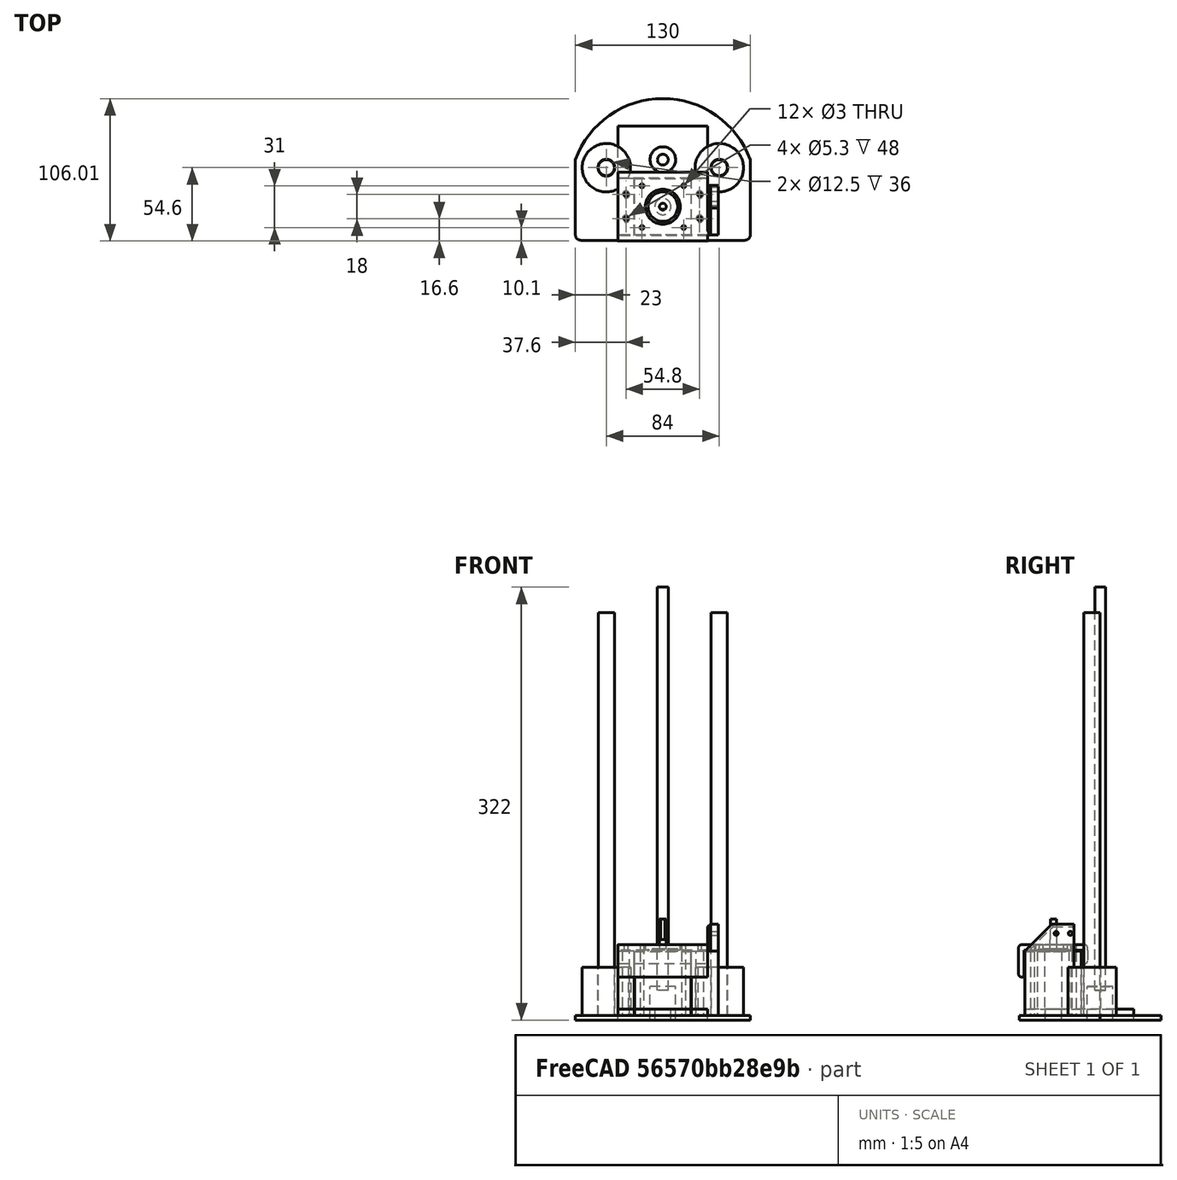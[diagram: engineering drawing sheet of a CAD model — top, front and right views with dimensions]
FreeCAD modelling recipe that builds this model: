
FCSTD DOCUMENT  (FreeCAD 0.18R16110 (Git))
Label: jSCARA-V2
License: All rights reserved
LicenseURL: http://en.wikipedia.org/wiki/All_rights_reserved
objects: PartDesign::Pad×12, Sketcher::SketchObject×7, Part::Cylinder×4, PartDesign::Fillet×3, PartDesign::Body×3, App::Part×3, PartDesign::Mirrored×2, Part::FeaturePython×2, PartDesign::Chamfer×2, Mesh::Feature×1, PartDesign::Pocket×1
note: 49 computed .brp shape members not serialized (recipe doc carries the construction recipe); baked Part::Feature solids carry a one-line shape summary decoded from their .brp

FEATURE [Sketcher::SketchObject] Sketch
  MapMode = 5
  Support = -> [XY_Plane]
  sketch-geometry (4):
    g0: LineSegment StartX=-65 StartY=-3e-15 StartZ=0 EndX=-65 EndY=-60 EndZ=0
    g1: LineSegment StartX=-65 StartY=-60 StartZ=0 EndX=65 EndY=-60 EndZ=0
    g2: LineSegment StartX=65 StartY=-60 StartZ=0 EndX=65 EndY=0 EndZ=0
    g3: ArcOfCircle CenterX=-9e-15 CenterY=-23.8163 CenterZ=0 NormalX=0 NormalY=0 NormalZ=1 AngleXU=0 Radius=69.2258 StartAngle=0.351214 EndAngle=2.79038
  constraints (11):
    c: Coincident(g0,g1)
    c: Coincident(g1,g2)
    c: Vertical(g2)
    c: Vertical(g0)
    c: Symmetric(g1,g0,g-2)
    c: DistanceX(g1,g1) = 130
    c: Coincident(g3,g2)
    c: Coincident(g3,g0)
    c: Equal(g0,g2)
    c: DistanceY(g2,g2) = 60
    c: PointOnObject(g2,g-1)
FEATURE [PartDesign::Pad] Pad  label="Base"
  Length = 3.4
  Length2 = 100
  Profile = -> Sketch
  Type = 0
FEATURE [Part::Cylinder] Cylinder  label="R Rail"
  Angle = 360
  AttacherType = Attacher::AttachEngine3D
  Height = 300
  Placement = pos=(42,-6,3) rot=(0,0,1;0rad)
  Radius = 6
FEATURE [Sketcher::SketchObject] Sketch001
  MapMode = 5
  Placement = pos=(0,0,3.4) rot=(0,0,1;0rad)
  Support = -> [Pad]
  sketch-geometry (2):
    g0: Circle CenterX=42 CenterY=-6 CenterZ=0 NormalX=0 NormalY=0 NormalZ=1 AngleXU=0 Radius=6.25
    g1: Circle CenterX=42 CenterY=-6 CenterZ=0 NormalX=0 NormalY=0 NormalZ=1 AngleXU=0 Radius=18
  constraints (5):
    c: Radius(g0) = 6.25
    c: Coincident(g1,g0)
    c: Radius(g1) = 18
    c: DistanceY(g0,g-1) = 6
    c: DistanceX(g-1,g0) = 42
FEATURE [PartDesign::Fillet] Fillet
  Base = -> Pad [Edge5,Edge2]
  BaseFeature = -> Pad
  Radius = 4
FEATURE [PartDesign::Pad] Pad001  label="Rod Holder R"
  BaseFeature = -> Fillet
  Length = 36
  Length2 = 100
  Profile = -> Sketch001
  Type = 0
FEATURE [PartDesign::Mirrored] Mirrored  label="Rod Holder L"
  BaseFeature = -> Pad001
  MirrorPlane = -> YZ_Plane
  Originals = -> [Pad001]
FEATURE [Part::FeaturePython] b_NEMASteppper__42x48__001_  label="NEMASteppper (42x48)_001"  # a2plus imported part (geometry in sourceFile) (typed FeaturePython)
  Placement = pos=(0,-35,3) rot=(0,0,1;0rad)
  a2p_Version = V0.1
  fixedPosition = true
  sourceFile = .\NEMASteppper (42x48).FCStd
  subassemblyImport = false
  timeLastImport = 1.55797e+09
  updateColors = true
FEATURE [Part::Cylinder] Cylinder001  label="L Rail"
  Angle = 360
  AttacherType = Attacher::AttachEngine3D
  Height = 300
  Placement = pos=(-42,-6,3) rot=(0,0,1;0rad)
  Radius = 6
FEATURE [Sketcher::SketchObject] Sketch002
  MapMode = 5
  Placement = pos=(0,0,3.4) rot=(0,0,1;0rad)
  Support = -> [Mirrored]
  sketch-geometry (7):
    g0: LineSegment StartX=-21.4 StartY=-56 StartZ=0 EndX=-21.4 EndY=-14 EndZ=0
    g1: LineSegment StartX=-21.4 StartY=-14 StartZ=0 EndX=-33.4 EndY=-14 EndZ=0
    g2: LineSegment StartX=-33.4 StartY=-14 StartZ=0 EndX=-33.4 EndY=-56 EndZ=0
    g3: LineSegment StartX=-33.4 StartY=-56 StartZ=0 EndX=-21.4 EndY=-56 EndZ=0
    g4: Circle CenterX=-27.4 CenterY=-26 CenterZ=0 NormalX=0 NormalY=0 NormalZ=1 AngleXU=0 Radius=2.65
    g5: Circle CenterX=-27.4 CenterY=-44 CenterZ=0 NormalX=0 NormalY=0 NormalZ=1 AngleXU=0 Radius=2.65
    g6: LineSegment [constr] StartX=-27.4 StartY=-14 StartZ=0 EndX=-27.4 EndY=-56 EndZ=0
  constraints (21):
    c: Vertical(g0)
    c: Coincident(g0,g1)
    c: Horizontal(g1)
    c: Coincident(g1,g2)
    c: Vertical(g2)
    c: Coincident(g2,g3)
    c: Coincident(g3,g0)
    c: Horizontal(g3)
    c: DistanceY(g0,g-1) = 14
    c: DistanceY(g0,g0) = 42
    c: DistanceX(g1,g1) = 12
    c: DistanceX(g0,g-1) = 21.4
    c: DistanceY(g4,g1) = 12
    c: Equal(g4,g5) = 3
    c: PointOnObject(g6,g1)
    c: Symmetric(g0,g2,g6)
    c: PointOnObject(g5,g6)
    c: PointOnObject(g4,g6)
    c: PointOnObject(g6,g3)
    c: DistanceY(g2,g5) = 12
    c: Diameter(g4) = 5.3
FEATURE [PartDesign::Pad] Pad002
  BaseFeature = -> Mirrored
  Length = 48
  Length2 = 100
  Profile = -> Sketch002
  Type = 0
FEATURE [PartDesign::Mirrored] Mirrored001
  BaseFeature = -> Pad002
  MirrorPlane = -> Sketch002 [V_Axis]
  Originals = -> [Pad002]
FEATURE [Sketcher::SketchObject] Sketch003
  MapMode = 5
  Support = -> [XY_Plane002]
  sketch-geometry (14):
    g0: Circle CenterX=-27.4 CenterY=-26 CenterZ=0 NormalX=0 NormalY=0 NormalZ=1 AngleXU=0 Radius=1.5
    g1: Circle CenterX=0 CenterY=-35 CenterZ=0 NormalX=0 NormalY=0 NormalZ=1 AngleXU=0 Radius=13
    g2: LineSegment StartX=-33.4 StartY=-14 StartZ=0 EndX=33.4 EndY=-14 EndZ=0
    g3: LineSegment StartX=33.4 StartY=-14 StartZ=0 EndX=33.4 EndY=-56 EndZ=0
    g4: LineSegment StartX=33.4 StartY=-56 StartZ=0 EndX=-33.4 EndY=-56 EndZ=0
    g5: LineSegment StartX=-33.4 StartY=-56 StartZ=0 EndX=-33.4 EndY=-14 EndZ=0
    g6: Circle CenterX=27.4 CenterY=-26 CenterZ=0 NormalX=0 NormalY=0 NormalZ=1 AngleXU=0 Radius=1.5
    g7: Circle CenterX=27.4 CenterY=-44 CenterZ=0 NormalX=0 NormalY=0 NormalZ=1 AngleXU=0 Radius=1.5
    g8: Circle CenterX=-27.4 CenterY=-44 CenterZ=0 NormalX=0 NormalY=0 NormalZ=1 AngleXU=0 Radius=1.5
    g9: LineSegment [constr] StartX=-27.4 StartY=-26 StartZ=0 EndX=-27.4 EndY=-44 EndZ=0
    g10: Circle CenterX=-15.5 CenterY=-50.5 CenterZ=0 NormalX=0 NormalY=0 NormalZ=1 AngleXU=0 Radius=1.5
    g11: Circle CenterX=15.5 CenterY=-50.5 CenterZ=0 NormalX=0 NormalY=0 NormalZ=1 AngleXU=0 Radius=1.5
    g12: Circle CenterX=-15.5 CenterY=-19.5 CenterZ=0 NormalX=0 NormalY=0 NormalZ=1 AngleXU=0 Radius=1.5
    g13: Circle CenterX=15.5 CenterY=-19.5 CenterZ=0 NormalX=0 NormalY=0 NormalZ=1 AngleXU=0 Radius=1.5
  constraints (36):
    c: PointOnObject(g1,g-2)
    c: Radius(g1) = 13
    c: DistanceY(g1,g-1) = 35
    c: Coincident(g2,g3)
    c: Coincident(g3,g4)
    c: Coincident(g4,g5)
    c: Coincident(g5,g2)
    c: Horizontal(g4)
    c: Vertical(g3)
    c: Vertical(g5)
    c: DistanceX(g2,g2) = 66.8
    c: Symmetric(g2,g2,g-2)
    c: DistanceY(g3,g3) = 42
    c: DistanceY(g2,g-1) = 14
    c: Equal(g0,g6) = 3
    c: Symmetric(g6,g0,g-2)
    c: Equal(g0,g8) = 3
    c: Equal(g8,g7) = 3
    c: DistanceY(g1,g6) = 9
    c: DistanceY(g8,g0) = 18
    c: Symmetric(g7,g8,g-2)
    c: Coincident(g9,g0)
    c: Coincident(g9,g8)
    c: Vertical(g9)
    c: Radius(g10) = 1.5
    c: Equal(g10,g11) = 3
    c: Symmetric(g10,g11,g-2)
    c: DistanceX(g10,g11) = 31
    c: DistanceY(g3,g11) = 5.5
    c: Equal(g10,g12) = 3
    c: Symmetric(g12,g13,g-2)
    c: DistanceX(g12,g13) = 31
    c: DistanceY(g10,g12) = 31
    c: Equal(g13,g12)
    c: DistanceX(g4,g8) = 6
    c: Radius(g0) = 1.5
FEATURE [PartDesign::Pad] Pad003
  Length = 4
  Length2 = 100
  Profile = -> Sketch003
  Type = 0
FEATURE [PartDesign::Fillet] Fillet002
  Base = -> Mirrored001 [Edge50,Edge37]
  BaseFeature = -> Mirrored001
  Radius = 2
FEATURE [PartDesign::Pad] Pad004
  BaseFeature = -> Pad003
  Length = 0.6
  Length2 = 100
  Profile = -> Pad003 [Face3]
  Type = 0
FEATURE [PartDesign::Pad] Pad005
  BaseFeature = -> Pad004
  Length = 4
  Length2 = 100
  Profile = -> Pad004 [Face19]
  Type = 0
FEATURE [PartDesign::Pad] Pad006
  BaseFeature = -> Pad005
  Length = 20
  Length2 = 100
  Profile = -> Pad005 [Face21]
  Type = 0
FEATURE [PartDesign::Pad] Pad007
  BaseFeature = -> Pad006
  Length = 0.6
  Length2 = 100
  Profile = -> Pad006 [Face1]
  Type = 0
FEATURE [PartDesign::Pad] Pad008
  BaseFeature = -> Pad007
  Length = 4
  Length2 = 100
  Profile = -> Pad007 [Face11]
  Type = 0
FEATURE [PartDesign::Pad] Pad009
  BaseFeature = -> Pad008
  Length = 10
  Length2 = 100
  Profile = -> Pad008 [Face28]
  Type = 0
FEATURE [PartDesign::Fillet] Fillet003
  Base = -> Pad009 [Edge83,Edge65,Edge75,Edge87]
  BaseFeature = -> Pad009
  Radius = 2
FEATURE [PartDesign::Body] Body001  label="Stepper Retainer"
  Group = -> [Sketch003,Pad003,Pad004,Pad005,Pad006,Pad007,Pad008,Pad009,Fillet003]
  Origin = -> Origin002
  Placement = pos=(0,0,52) rot=(0,0,1;0rad)
  Tip = -> Fillet003
FEATURE [Mesh::Feature] KW12_3_Microswitch  label="KW12-3 Microswitch"
  Placement = pos=(48,-15,58) rot=(-0.57735,0.57735,0.57735;4.18879rad)
FEATURE [Part::Cylinder] Cylinder002  label="Lead Screw Coupler"
  Angle = 360
  AttacherType = Attacher::AttachEngine3D
  Height = 25
  Radius = 9.5
FEATURE [Sketcher::SketchObject] Sketch004
  ExternalGeometry = -> [Fillet002]
  MapMode = 5
  Placement = pos=(0,0,3.4) rot=(0,0,1;0rad)
  Support = -> [Fillet002]
  sketch-geometry (4):
    g0: LineSegment StartX=33.4 StartY=-19.3196 StartZ=0 EndX=41.4 EndY=-19.3196 EndZ=0
    g1: LineSegment StartX=41.4 StartY=-19.3196 StartZ=0 EndX=41.4 EndY=-56 EndZ=0
    g2: LineSegment StartX=41.4 StartY=-56 StartZ=0 EndX=33.4 EndY=-56 EndZ=0
    g3: LineSegment StartX=33.4 StartY=-56 StartZ=0 EndX=33.4 EndY=-19.3196 EndZ=0
  constraints (10):
    c: Coincident(g0,g1)
    c: Coincident(g1,g2)
    c: Coincident(g2,g3)
    c: Coincident(g3,g0)
    c: Horizontal(g0)
    c: Horizontal(g2)
    c: Vertical(g1)
    c: Vertical(g3)
    c: Coincident(g2,g-3)
    c: DistanceX(g0,g0) = 8
FEATURE [PartDesign::Pad] Pad010
  BaseFeature = -> Fillet002
  Length = 68
  Length2 = 100
  Profile = -> Sketch004
  Type = 0
FEATURE [PartDesign::Chamfer] Chamfer
  Base = -> Pad010 [Edge72]
  BaseFeature = -> Pad010
  Size = 20
FEATURE [PartDesign::Chamfer] Chamfer001
  Base = -> Chamfer [Edge12,Edge33]
  BaseFeature = -> Chamfer
  Size = 2
FEATURE [Sketcher::SketchObject] Sketch005
  MapMode = 5
  Placement = pos=(41.4,0,0) rot=(0.57735,0.57735,0.57735;2.0944rad)
  Support = -> [Chamfer001]
  sketch-geometry (3):
    g0: Circle CenterX=-32.7462 CenterY=64.4514 CenterZ=0 NormalX=0 NormalY=0 NormalZ=1 AngleXU=0 Radius=1.5
    g1: Circle CenterX=-22.2462 CenterY=64.4514 CenterZ=0 NormalX=0 NormalY=0 NormalZ=1 AngleXU=0 Radius=1.5
    g2: LineSegment [constr] StartX=-32.7462 StartY=64.4514 StartZ=0 EndX=-22.2462 EndY=64.4514 EndZ=0
  constraints (6):
    c: Radius(g0) = 1.5
    c: Horizontal(g2)
    c: Coincident(g2,g0)
    c: Coincident(g2,g1)
    c: Equal(g1,g0)
    c: DistanceX(g2,g2) = 10.5
FEATURE [PartDesign::Pocket] Pocket
  BaseFeature = -> Chamfer001
  Length = 10
  Length2 = 0
  Profile = -> Sketch005
  Type = 0
FEATURE [PartDesign::Body] Body  label="Base Plate"
  Group = -> [Sketch,Pad,Sketch001,Fillet,Pad001,Mirrored,Sketch002,Pad002,Mirrored001,Fillet002,Sketch004,Pad010,Chamfer,Chamfer001,Sketch005,Pocket]
  Origin = -> Origin
  Tip = -> Pocket
FEATURE [App::Part] Part  label="Base Assembly"
  Group = -> [Cylinder001,Cylinder,Body,b_NEMASteppper__42x48__001_,Body001,KW12_3_Microswitch]
  Origin = -> Origin001
FEATURE [Part::Cylinder] Cylinder003  label="Lead Screw"
  Angle = 360
  AttacherType = Attacher::AttachEngine3D
  Height = 300
  Placement = pos=(0,0,22) rot=(0,0,1;0rad)
  Radius = 4
FEATURE [App::Part] Part001  label="Z Screw"
  Group = -> [Cylinder003,Cylinder002]
  Origin = -> Origin003
  Placement = pos=(0,-35,61) rot=(0,0,1;0rad)
FEATURE [Sketcher::SketchObject] Sketch006
  MapMode = 5
  Support = -> [XY_Plane005]
  sketch-geometry (5):
    g0: LineSegment StartX=-33.3207 StartY=25 StartZ=0 EndX=33.3207 EndY=25 EndZ=0
    g1: LineSegment StartX=33.3207 StartY=25 StartZ=0 EndX=33.3207 EndY=-56 EndZ=0
    g2: LineSegment StartX=33.3207 StartY=-56 StartZ=0 EndX=-33.3207 EndY=-56 EndZ=0
    g3: LineSegment StartX=-33.3207 StartY=-56 StartZ=0 EndX=-33.3207 EndY=25 EndZ=0
    g4: Circle CenterX=0 CenterY=-35.0087 CenterZ=0 NormalX=0 NormalY=0 NormalZ=1 AngleXU=0 Radius=6
  constraints (12):
    c: Coincident(g0,g1)
    c: Coincident(g1,g2)
    c: Coincident(g2,g3)
    c: Coincident(g3,g0)
    c: Horizontal(g2)
    c: Vertical(g1)
    c: Vertical(g3)
    c: Symmetric(g0,g0,g-2)
    c: DistanceY(g2,g-1) = 56
    c: DistanceY(g-1,g0) = 25
    c: Radius(g4) = 6
    c: PointOnObject(g4,g-2)
FEATURE [PartDesign::Pad] Pad011
  Length = 8
  Length2 = 100
  Profile = -> Sketch006
  Type = 0
FEATURE [PartDesign::Body] Body002
  Group = -> [Sketch006,Pad011]
  Origin = -> Origin005
  Tip = -> Pad011
FEATURE [Part::FeaturePython] b_NEMASteppper__42x48__001_001  label="NEMASteppper (42x48)_002"  # a2plus imported part (geometry in sourceFile) (typed FeaturePython)
  Placement = pos=(0,-35,3) rot=(0,0,1;0rad)
  a2p_Version = V0.1
  fixedPosition = true
  sourceFile = .\NEMASteppper (42x48).FCStd
  subassemblyImport = false
  timeLastImport = 1.55797e+09
  updateColors = true
FEATURE [App::Part] Part002  label="Carriage"
  Group = -> [Body002,b_NEMASteppper__42x48__001_001]
  Origin = -> Origin004
  Placement = pos=(0,0,120) rot=(0,0,1;0rad)
